# Revit family: Prises verrouillés 200_250V
name_source: partatom
category: Installations électriques
revit_build: Autodesk Revit 2018 (Build: 20170223_1515(x64)
units: mm (PartAtom-declared; Revit-internal decimal feet)

## family parameters
Conserver l'orientation des annotations = Non
Cote de connecteur circulaire = Utiliser le diamètre
Couper avec des vides une fois chargée = Non
Hôte = Face
Partagée = Non
Point de calcul de pièce = Non
Type d'élément = Normal

## types (2) — shared parameters
Couleur caractéristique = bleu
Elévation par défaut = 1000 mm  [stored 3.28084 ft]
Fabricant = Legrand
Famille produit = 0852-P17
Intensité A = 16 A
Nombre de pôles = 3
Position de la Terre h = 6
Prise au standard international pour montage encastré ou saillie avec accessoire permet la connexion d'appareils de puissance = Prise au standard international pour montage encastré ou saillie avec accessoire permet la connexion d'appareils de puissance
Standard CEI ou NFC = CEI
Température maximum d'utilisation = +40
Température minimum d'utilisation = -25
Tension V = 230 V  50/60 Hz  bleu
Type de cerrouillage = verrouillage électromécanique
entraxe de fixation horizontal mm = 91 mm
entraxe de fixation vertical mm = 87 mm
hauteur mm = 105 mm  [stored 0.344488 ft]
largeur mm = 125 mm  [stored 0.410105 ft]
matériau du boitier = plastique
profondeur d'encastrement mm = 81 mm  [stored 0.265748 ft]
profondeur mm = 120 mm  [stored 0.393701 ft]
sans halogène = Oui
type de raccordement = bornes à vis

## per-type parameters (varying)
| type | Description | Modèle | classe de protection IP | résistance aux chocs IK |
| P17 - IP44 - 200/250V - 16A -2P+T | LG-057320 Prise vérrouillée P17 - IP55 - 200/250V - 16A -2P+T | LG-057320 | IP55 | 11 |
| P17 - IP55 - 200/250V - 16A -2P+T | LG-057300 Prise vérrouillée P17 - IP44 - 200/250V - 16A -2P+T | LG-057300 | IP44 | 08 |

note: [stored X ft] marks values corroborated as IEEE doubles in the binary element streams (Revit-internal decimal feet)
